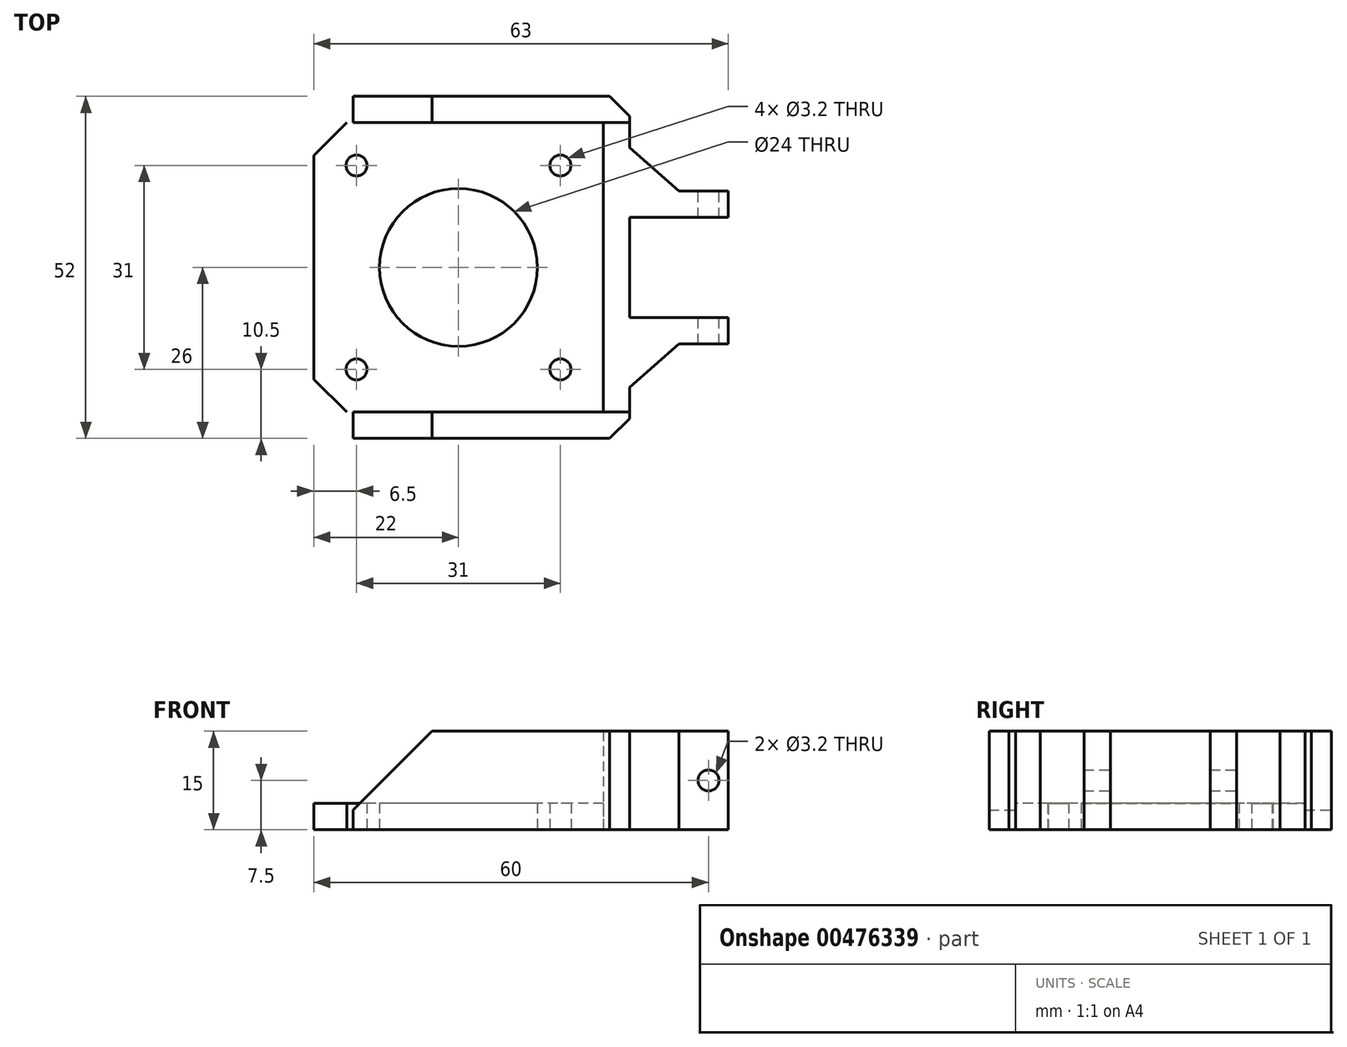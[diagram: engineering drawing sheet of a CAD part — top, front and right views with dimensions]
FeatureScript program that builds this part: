
annotation { "Feature Type Name" : "Feature", "Feature Type Description" : "" }
export const myFeature = defineFeature(function(context is Context, id is Id, definition is map)
    precondition{}
    {
        {
            var Q0;
            Q0=qCreatedBy(makeId("Top.planeOp"),FACE);
            var sketch = newSketch(context, id + "F0", { "sketchPlane" : qUnion([Q0])});
            skLineSegment(sketch, "E0.bottom", {"start": v(22, 22) * mm, "end": v(-22, 22) * mm});
            skLineSegment(sketch, "E0.top", {"start": v(22, -22) * mm, "end": v(-22, -22) * mm});
            skLineSegment(sketch, "E0.left", {"start": v(22, 22) * mm, "end": v(22, -22) * mm});
            skLineSegment(sketch, "E0.right", {"start": v(-22, 22) * mm, "end": v(-22, -22) * mm});
            skPoint(sketch, "E0.middle", {"position": v(0, 0) * mm});
            skCircle(sketch, "E1", {"center": v(0, 0) * mm, "radius": 12 * mm});
            skCircle(sketch, "E2", {"center": v(-15.5, 15.5) * mm, "radius": 1.6 * mm});
            skCircle(sketch, "E3", {"center": v(-15.5, -15.5) * mm, "radius": 1.6 * mm});
            skCircle(sketch, "E4", {"center": v(15.5, 15.5) * mm, "radius": 1.6 * mm});
            skCircle(sketch, "E5", {"center": v(15.5, -15.5) * mm, "radius": 1.6 * mm});
            skSolve(sketch);
        }
        {
            var Q0;
            Q0=makeQuery(id+"F0.imprint","IMPRINT",FACE,{"disambiguationData":[TD([[makeQuery(id+"F0.imprint","IMPRINT",EDGE,{"derivedFrom":sQuery(id+"F0.wireOp",EDGE,"E0.bottom")}),1.0]])]});
            extrude(context, id + "F1", {"entities" : qUnion([Q0]), "depth" : 4 * mm});
        }
        {
            var Q0;
            Q0=makeQuery(id+"F1.opExtrude","SWEPT_EDGE",EDGE,{"disambiguationData":[OSD([sQuery(id+"F0.wireOp",EDGE,"E0.bottom"),sQuery(id+"F0.wireOp",EDGE,"E0.right")])]});
            var Q1;
            Q1=makeQuery(id+"F1.opExtrude","SWEPT_EDGE",EDGE,{"disambiguationData":[OSD([sQuery(id+"F0.wireOp",EDGE,"E0.top"),sQuery(id+"F0.wireOp",EDGE,"E0.right")])]});
            chamfer(context, id + "F2", {"entities" : qUnion([Q0, Q1]), "width" : 5 * mm, "tangentPropagation" : true});
        }
        {
            var Q0;
            Q0=qCreatedBy(makeId("Top.planeOp"),FACE);
            var sketch = newSketch(context, id + "F3", { "sketchPlane" : qUnion([Q0])});
            skLineSegment(sketch, "E6", {"start": v(0, 0) * mm, "end": v(26, 0) * mm});
            skLineSegment(sketch, "E7", {"start": v(26, 0) * mm, "end": v(26, 7.6) * mm});
            skLineSegment(sketch, "E8", {"start": v(26, 0) * mm, "end": v(26, -7.6) * mm});
            skLineSegment(sketch, "E9", {"start": v(26, -7.6) * mm, "end": v(41, -7.6) * mm});
            skLineSegment(sketch, "E10", {"start": v(26, 7.6) * mm, "end": v(41, 7.6) * mm});
            skLineSegment(sketch, "E11", {"start": v(41, -7.6) * mm, "end": v(41, -11.6) * mm});
            skLineSegment(sketch, "E12", {"start": v(41, -11.6) * mm, "end": v(26, -11.6) * mm});
            skLineSegment(sketch, "E13", {"start": v(41, 7.6) * mm, "end": v(41, 11.6) * mm});
            skLineSegment(sketch, "E14", {"start": v(41, 11.6) * mm, "end": v(26, 11.6) * mm});
            skLineSegment(sketch, "E15", {"start": v(26, 11.6) * mm, "end": v(26, 7.6) * mm});
            skLineSegment(sketch, "E16", {"start": v(26, -7.6) * mm, "end": v(26, -11.6) * mm});
            skLineSegment(sketch, "E17", {"start": v(26, -11.6) * mm, "end": v(26, -18.97) * mm});
            skLineSegment(sketch, "E18", {"start": v(33.5, -11.6) * mm, "end": v(26, -18.21) * mm});
            skLineSegment(sketch, "E19", {"start": v(26, 11.6) * mm, "end": v(26, 21.6) * mm});
            skLineSegment(sketch, "E20", {"start": v(33.5, 11.6) * mm, "end": v(26, 18.21) * mm});
            skLineSegment(sketch, "E21", {"start": v(0, 0) * mm, "end": v(22, 0) * mm});
            skLineSegment(sketch, "E22", {"start": v(22, 0) * mm, "end": v(22, -22) * mm});
            skLineSegment(sketch, "E23", {"start": v(22, 0) * mm, "end": v(22, 22) * mm});
            skLineSegment(sketch, "E24", {"start": v(22, 22) * mm, "end": v(29.23, 22) * mm});
            skLineSegment(sketch, "E25", {"start": v(26, 21.6) * mm, "end": v(26, 22) * mm});
            skLineSegment(sketch, "E26", {"start": v(22, -22) * mm, "end": v(29.27, -22) * mm});
            skLineSegment(sketch, "E27", {"start": v(26, -18.97) * mm, "end": v(26, -22) * mm});
            skPoint(sketch, "E27.endSnap0", {"position": v(25.63, -22) * mm});
            skLineSegment(sketch, "E28", {"start": v(-14, -22) * mm, "end": v(25.63, -22) * mm});
            skSolve(sketch);
        }
        {
            var Q0;
            Q0=makeQuery(id+"F3.imprint","IMPRINT",FACE,{"disambiguationData":[TD([[makeQuery(id+"F3.imprint","IMPRINT",EDGE,{"derivedFrom":sQuery(id+"F3.wireOp",EDGE,"E10")}),1.0]])]});
            var Q1;
            {var subQ3=sQuery(id+"F3.wireOp",EDGE,"E20");Q1=makeQuery(id+"F3.imprint","IMPRINT",FACE,{"disambiguationData":[TD([[makeQuery(id+"F3.imprint","IMPRINT",EDGE,{"derivedFrom":subQ3}),1.0]])]});}
            var Q2;
            Q2=makeQuery(id+"F3.imprint","IMPRINT",FACE,{"disambiguationData":[TD([[makeQuery(id+"F3.imprint","IMPRINT",EDGE,{"derivedFrom":sQuery(id+"F3.wireOp",EDGE,"E9")}),-1.0]])]});
            var Q3;
            {var subQ3=sQuery(id+"F3.wireOp",EDGE,"E18");Q3=makeQuery(id+"F3.imprint","IMPRINT",FACE,{"disambiguationData":[TD([[makeQuery(id+"F3.imprint","IMPRINT",EDGE,{"derivedFrom":subQ3}),-1.0]])]});}
            var Q4;
            Q4=makeQuery(id+"F3.imprint","IMPRINT",FACE,{"disambiguationData":[TD([[makeQuery(id+"F3.imprint","IMPRINT",EDGE,{"derivedFrom":sQuery(id+"F3.wireOp",EDGE,"E6")}),-1.0]])]});
            var Q5;
            Q5=makeQuery(id+"F3.imprint","IMPRINT",FACE,{"disambiguationData":[TD([[makeQuery(id+"F3.imprint","IMPRINT",EDGE,{"derivedFrom":sQuery(id+"F3.wireOp",EDGE,"E6")}),1.0]])]});
            extrude(context, id + "F4", {"entities" : qUnion([Q0, Q1, Q2, Q3, Q4, Q5]), "depth" : 15 * mm});
        }
        {
            var Q0;
            Q0=makeQuery(id+"F1.opExtrude","CAP_FACE",FACE,{"disambiguationData":[OSD([sQuery(id+"F0.wireOp",EDGE,"E0.bottom"),sQuery(id+"F0.wireOp",EDGE,"E0.top"),sQuery(id+"F0.wireOp",EDGE,"E0.left"),sQuery(id+"F0.wireOp",EDGE,"E0.right"),sQuery(id+"F0.wireOp",EDGE,"E1"),sQuery(id+"F0.wireOp",EDGE,"E2"),sQuery(id+"F0.wireOp",EDGE,"E3"),sQuery(id+"F0.wireOp",EDGE,"E4"),sQuery(id+"F0.wireOp",EDGE,"E5")])],"isStart":true});
            var sketch = newSketch(context, id + "F5", { "sketchPlane" : qUnion([Q0])});
            skLineSegment(sketch, "E29", {"start": v(22, -22) * mm, "end": v(22, -26) * mm});
            skLineSegment(sketch, "E30", {"start": v(22, -26) * mm, "end": v(26, -26) * mm});
            skLineSegment(sketch, "E31", {"start": v(26, -26) * mm, "end": v(26, -22) * mm});
            skLineSegment(sketch, "E32", {"start": v(22, 22) * mm, "end": v(22, 26) * mm});
            skLineSegment(sketch, "E33", {"start": v(22, 26) * mm, "end": v(26, 26) * mm});
            skLineSegment(sketch, "E34", {"start": v(26, 26) * mm, "end": v(26, 22) * mm});
            skLineSegment(sketch, "E35", {"start": v(26, 22) * mm, "end": v(22, 22) * mm});
            skLineSegment(sketch, "E36", {"start": v(22, 22) * mm, "end": v(-16, 22) * mm});
            skLineSegment(sketch, "E37", {"start": v(-16, 22) * mm, "end": v(-16, 26) * mm});
            skLineSegment(sketch, "E38", {"start": v(-16, 26) * mm, "end": v(22, 26) * mm});
            skLineSegment(sketch, "E39", {"start": v(22, -26) * mm, "end": v(-16, -26) * mm});
            skLineSegment(sketch, "E40", {"start": v(-16, -26) * mm, "end": v(-16, -22) * mm});
            skLineSegment(sketch, "E41", {"start": v(-16, -22) * mm, "end": v(22, -22) * mm});
            skLineSegment(sketch, "E42", {"start": v(26, -22) * mm, "end": v(22, -22) * mm});
            skSolve(sketch);
        }
        {
            var Q0;
            Q0 = qSketchRegion(id + "F5", true);
            extrude(context, id + "F6", {"entities" : qUnion([Q0]), "oppositeDirection" : true, "depth" : 15 * mm});
        }
        {
            var Q0;
            Q0=makeQuery(id+"F6.opExtrude","CAP_EDGE",EDGE,{"disambiguationData":[OSD([sQuery(id+"F5.wireOp",EDGE,"E37")])],"isStart":false});
            var Q1;
            Q1=makeQuery(id+"F6.opExtrude","CAP_EDGE",EDGE,{"disambiguationData":[OSD([sQuery(id+"F5.wireOp",EDGE,"E40")])],"isStart":false});
            chamfer(context, id + "F7", {"entities" : qUnion([Q0, Q1]), "width" : 12 * mm, "tangentPropagation" : true});
        }
        {
            var Q0;
            Q0=makeQuery(id+"F4.opExtrude","SWEPT_FACE",FACE,{"disambiguationData":[OSD([sQuery(id+"F3.wireOp",EDGE,"E14")])]});
            var sketch = newSketch(context, id + "F8", { "sketchPlane" : qUnion([Q0])});
            skLineSegment(sketch, "E43", {"start": v(-41, 7.5) * mm, "end": v(-38, 7.5) * mm});
            skCircle(sketch, "E44", {"center": v(-38, 7.5) * mm, "radius": 1.6 * mm});
            skSolve(sketch);
        }
        {
            var Q0;
            Q0=makeQuery(id+"F8.imprint","IMPRINT",FACE,{"disambiguationData":[TD([[makeQuery(id+"F8.imprint","IMPRINT",EDGE,{"derivedFrom":sQuery(id+"F8.wireOp",EDGE,"E44")}),1.0]])]});
            extrude(context, id + "F9", {"entities" : qUnion([Q0]), "operationType" : NewBodyOperationType.REMOVE, "oppositeDirection" : true, "depth" : 25 * mm});
        }
        {
            var Q0;
            Q0=makeQuery(id+"F6.opExtrude","SWEPT_EDGE",EDGE,{"disambiguationData":[OSD([sQuery(id+"F5.wireOp",EDGE,"E33"),sQuery(id+"F5.wireOp",EDGE,"E34")])]});
            var Q1;
            Q1=makeQuery(id+"F6.opExtrude","SWEPT_EDGE",EDGE,{"disambiguationData":[OSD([sQuery(id+"F5.wireOp",EDGE,"E30"),sQuery(id+"F5.wireOp",EDGE,"E31")])]});
            chamfer(context, id + "F10", {"entities" : qUnion([Q0, Q1]), "width" : 3 * mm, "tangentPropagation" : true});
        }
    });
